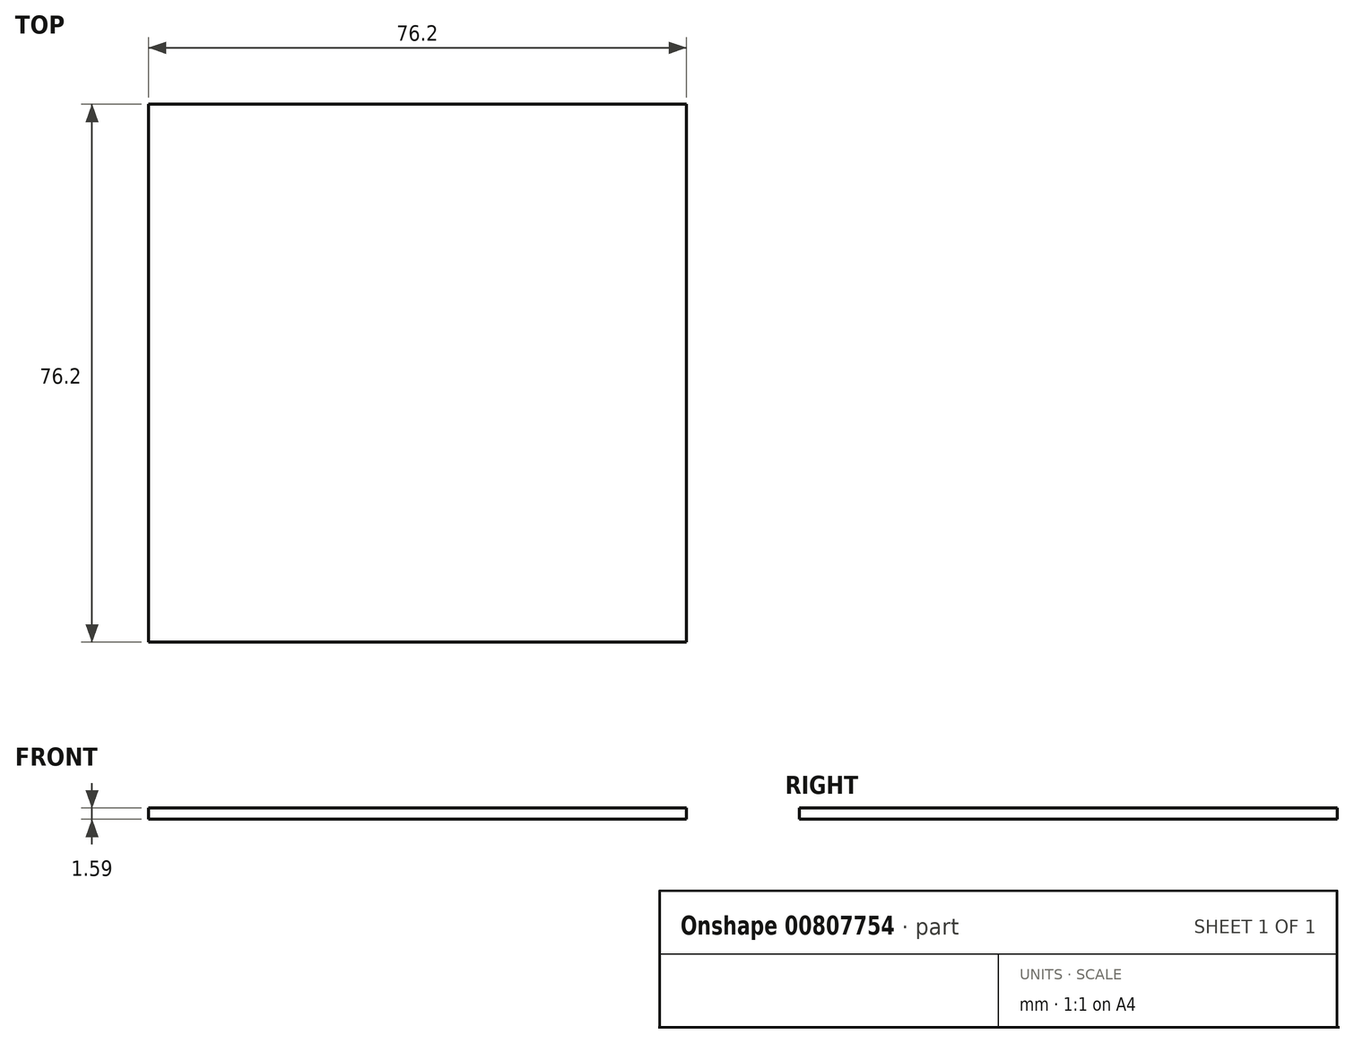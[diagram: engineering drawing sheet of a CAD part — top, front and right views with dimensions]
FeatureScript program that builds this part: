
annotation { "Feature Type Name" : "Feature", "Feature Type Description" : "" }
export const myFeature = defineFeature(function(context is Context, id is Id, definition is map)
    precondition{}
    {
        {
            var Q0;
            Q0=qCreatedBy(makeId("Top.planeOp"),FACE);
            var sketch = newSketch(context, id + "F0", { "sketchPlane" : qUnion([Q0])});
            skLineSegment(sketch, "E0", {"start": v(38.1, -63.5) * mm, "end": v(38.1, 12.7) * mm});
            skLineSegment(sketch, "E1", {"start": v(38.1, 12.7) * mm, "end": v(-38.1, 12.7) * mm});
            skLineSegment(sketch, "E2", {"start": v(-38.1, 12.7) * mm, "end": v(-38.1, -63.5) * mm});
            skLineSegment(sketch, "E3", {"start": v(-38.1, -63.5) * mm, "end": v(38.1, -63.5) * mm});
            skSolve(sketch);
        }
        {
            var Q0;
            Q0=makeQuery(id+"F0.imprint","IMPRINT",FACE,{"disambiguationData":[TD([[makeQuery(id+"F0.imprint","IMPRINT",EDGE,{"derivedFrom":sQuery(id+"F0.wireOp",EDGE,"E0")}),1.0]])]});
            extrude(context, id + "F1", {"entities" : qUnion([Q0]), "depth" : 1.59 * mm, "offsetDistance" : 25.4 * mm});
        }
    });
